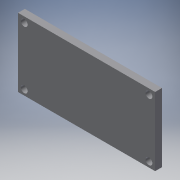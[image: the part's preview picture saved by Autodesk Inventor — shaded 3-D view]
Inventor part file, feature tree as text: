
AUTODESK INVENTOR PART (.ipt)
format: ipt  version: 2018.3 (Build 223284000, 284)  size: 174,592 bytes
history: native  units: mm
features: sketch x3, extrude x2, chamfer x1, hole x1
ambient origin geometry x8: Origin, YZ Plane, XZ Plane, XY Plane, X Axis, Y Axis, Z Axis, Center Point
bodies: Solid1 (feature_tree)
feature tree (7):
  extrude  "Extrusion1"  Depth=5.0mm
  extrude  "Extrusion2"  Depth=50.0mm
  chamfer  "Chamfer1"  Distance=18.0mm
  hole  "Hole2"  [1 undecoded]
  sketch  "Sketch1"  dims[d0=100.0mm d1=5.0mm]
  sketch  "Sketch2"  dims[d2=50.0mm d3=0.0mm d4=20.0mm]
  sketch  "Sketch3"  dims[d5=14.0mm d6=18.0mm d7=18.0mm d8=40.0mm d9=40.0mm d11=1.13mm d12=1.45mm d13=1.45mm d15=1.13mm d16=1.13mm d17=1.1mm d18=1.1mm d19=1.13mm d28=2.15mm d29=2.15mm d30=4.83298mm d31=2.15mm d32=2.15mm d33=4.83298mm d34=4.5mm d35=0.0mm d36=0.5mm d37=2.0mm d38=45.0deg d46=4.5mm d47=4.5mm d48=4.0mm d49=4.0mm d50=5.0mm d51=6.0mm d52=4.0mm d53=2.0mm d54=90.0deg d55=8.0mm d56=20.594885mm d57=4.5mm d58=4.5mm d59=4.0mm d60=4.0mm]
note: 1 required parameter value undecoded (feature->parameter linkage not recoverable at this tier; creation-order binding heuristic only, values carry confidence <= 0.55)
